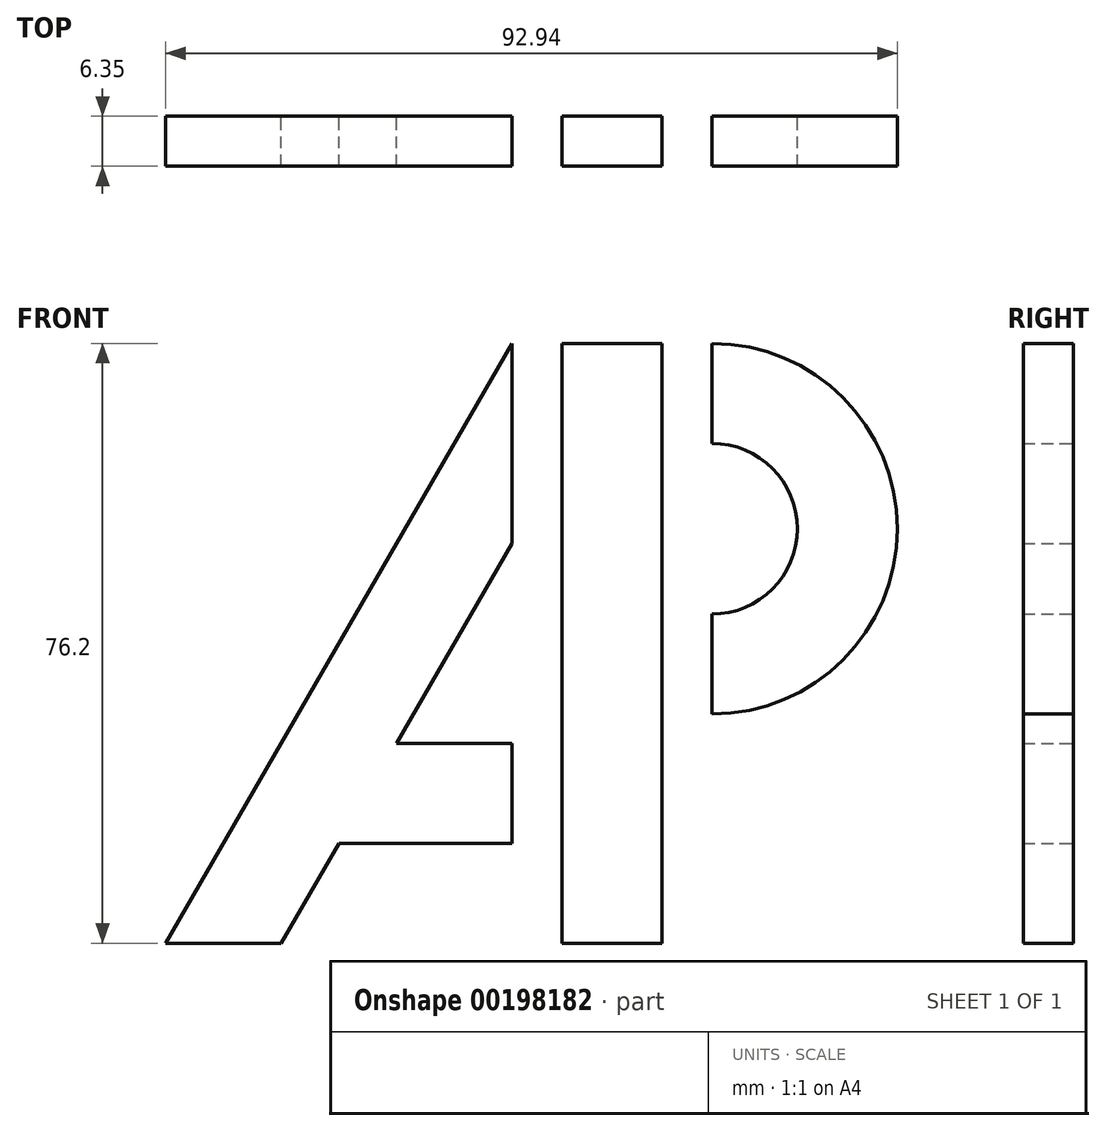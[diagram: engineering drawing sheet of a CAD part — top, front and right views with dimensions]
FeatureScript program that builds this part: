
annotation { "Feature Type Name" : "Feature", "Feature Type Description" : "" }
export const myFeature = defineFeature(function(context is Context, id is Id, definition is map)
    precondition{}
    {
        {
            var Q0;
            Q0=qCreatedBy(makeId("Front.planeOp"),FACE);
            var sketch = newSketch(context, id + "F0", { "sketchPlane" : qUnion([Q0])});
            skLineSegment(sketch, "E0.bottom", {"start": v(-6.35, 38.1) * mm, "end": v(6.35, 38.1) * mm});
            skLineSegment(sketch, "E0.top", {"start": v(-6.35, -38.1) * mm, "end": v(6.35, -38.1) * mm});
            skLineSegment(sketch, "E0.left", {"start": v(-6.35, 38.1) * mm, "end": v(-6.35, -38.1) * mm});
            skLineSegment(sketch, "E0.right", {"start": v(6.35, 38.1) * mm, "end": v(6.35, -38.1) * mm});
            skPoint(sketch, "E0.middle", {"position": v(0, 0) * mm});
            skLineSegment(sketch, "E1.bottom", {"start": v(6.35, 38.1) * mm, "end": v(12.7, 38.1) * mm});
            skLineSegment(sketch, "E1.top", {"start": v(6.35, 25.4) * mm, "end": v(12.7, 25.4) * mm});
            skLineSegment(sketch, "E1.left", {"start": v(6.35, 38.1) * mm, "end": v(6.35, 25.4) * mm});
            skLineSegment(sketch, "E1.right", {"start": v(12.7, 38.1) * mm, "end": v(12.7, 25.4) * mm});
            skLineSegment(sketch, "E2.bottom", {"start": v(6.35, 3.7) * mm, "end": v(12.7, 3.7) * mm});
            skLineSegment(sketch, "E2.top", {"start": v(6.35, -9) * mm, "end": v(12.7, -9) * mm});
            skLineSegment(sketch, "E2.left", {"start": v(6.35, 3.7) * mm, "end": v(6.35, -9) * mm});
            skLineSegment(sketch, "E2.right", {"start": v(12.7, 3.7) * mm, "end": v(12.7, -9) * mm});
            skLineSegment(sketch, "E3.bottom", {"start": v(-6.35, 38.1) * mm, "end": v(-12.7, 38.1) * mm});
            skLineSegment(sketch, "E3.top", {"start": v(-6.35, 12.7) * mm, "end": v(-12.7, 12.7) * mm});
            skLineSegment(sketch, "E3.left", {"start": v(-6.35, 38.1) * mm, "end": v(-6.35, 12.7) * mm});
            skLineSegment(sketch, "E3.right", {"start": v(-12.7, 38.1) * mm, "end": v(-12.7, 12.7) * mm});
            skLineSegment(sketch, "E4.bottom", {"start": v(-6.35, -38.1) * mm, "end": v(-12.7, -38.1) * mm});
            skLineSegment(sketch, "E4.top", {"start": v(-6.35, -25.4) * mm, "end": v(-12.7, -25.4) * mm});
            skLineSegment(sketch, "E4.left", {"start": v(-6.35, -38.1) * mm, "end": v(-6.35, -25.4) * mm});
            skLineSegment(sketch, "E4.right", {"start": v(-12.7, -38.1) * mm, "end": v(-12.7, -25.4) * mm});
            skArc(sketch, "E5", {"start": v(12.7, 3.7) * mm, "mid": v(23.55, 14.55) * mm, "end": v(12.7, 25.4) * mm});
            skArc(sketch, "E6", {"start": v(12.7, -9) * mm, "mid": v(36.25, 14.55) * mm, "end": v(12.7, 38.1) * mm});
            skLineSegment(sketch, "E7", {"start": v(-12.7, -38.1) * mm, "end": v(-56.7, -38.1) * mm});
            skLineSegment(sketch, "E8", {"start": v(-56.7, -38.1) * mm, "end": v(-12.7, 38.1) * mm});
            skLineSegment(sketch, "E9", {"start": v(-12.7, 12.7) * mm, "end": v(-34.7, -25.4) * mm});
            skLineSegment(sketch, "E10", {"start": v(-34.7, -25.4) * mm, "end": v(-12.7, -25.4) * mm});
            skLineSegment(sketch, "E11", {"start": v(-12.7, -25.4) * mm, "end": v(-12.7, -12.7) * mm});
            skLineSegment(sketch, "E12", {"start": v(-12.7, -12.7) * mm, "end": v(-6.35, -12.7) * mm});
            skLineSegment(sketch, "E13", {"start": v(-12.7, -12.7) * mm, "end": v(-27.36, -12.7) * mm});
            skLineSegment(sketch, "E14", {"start": v(-34.7, -25.4) * mm, "end": v(-42.03, -38.1) * mm});
            skSolve(sketch);
        }
        {
            var Q0;
            Q0=makeQuery(id+"F0.imprint","IMPRINT",FACE,{"disambiguationData":[TD([[makeQuery(id+"F0.imprint","IMPRINT",EDGE,{"derivedFrom":sQuery(id+"F0.wireOp",EDGE,"E3.right")}),-1.0]])]});
            var Q1;
            Q1=makeQuery(id+"F0.imprint","IMPRINT",FACE,{"disambiguationData":[TD([[makeQuery(id+"F0.imprint","IMPRINT",EDGE,{"derivedFrom":sQuery(id+"F0.wireOp",EDGE,"E0.bottom")}),-1.0]])]});
            var Q2;
            Q2=makeQuery(id+"F0.imprint","IMPRINT",FACE,{"disambiguationData":[TD([[makeQuery(id+"F0.imprint","IMPRINT",EDGE,{"derivedFrom":sQuery(id+"F0.wireOp",EDGE,"E1.right")}),1.0]])]});
            var Q3;
            {var subQ0=sQuery(id+"F0.wireOp",EDGE,"E10");Q3=makeQuery(id+"F0.imprint","IMPRINT",FACE,{"disambiguationData":[TD([[makeQuery(id+"F0.imprint","IMPRINT",EDGE,{"derivedFrom":subQ0}),1.0]])]});}
            extrude(context, id + "F1", {"entities" : qUnion([Q0, Q1, Q2, Q3]), "depth" : 6.35 * mm});
        }
    });
